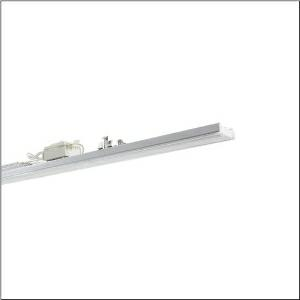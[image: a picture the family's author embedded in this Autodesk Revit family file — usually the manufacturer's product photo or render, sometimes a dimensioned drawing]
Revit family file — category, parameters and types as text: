
# Revit family: licross_21_recessed_mo_51te11vn48xg
name_source: partatom
category: Lighting Fixtures
units: mm (PartAtom-declared; Revit-internal decimal feet)

## family parameters
Cut with Voids When Loaded = No
Host = Face
Light Source = No
Part Type = Normal
Room Calculation Point = No
Round Connector Dimension = Use Diameter
Shared = No

## types (1)
- --- (1 x LED, 8000 lm, 44.1 W, 4000K)
    Apparent Load = 44 VA
    CIE Flux Codes = 89 96 99 100 100
    Color Rendering = 80
    Color Temperature = 4000K
    Default Elevation = 1800 mm
    Description = Licross 21 Recessed MO, luminaire insert, of sheet steel, galvanised, coil coated, white, length: 1.500mm, width: 66mm, height: 67mm, LED rated luminous flux: 8.000lm, light colour: 840, SDCM (Standard Deviation of Colour Matching)MacAdam ≤ 2 SDCM (initial), control gear: DALI 2, CLO, with plug, 5-pole, with phase selection, mains connection: 220..240V, AC, 50/60Hz, start of lifetime: 44W, end of service life: 48W, internal wiring halogen-free, primary light control with lens, of plastic, primary optical cover: cover, of PMMA, light emission: direct distribution, primary light characteristic: symmetric, protection rating (complete): IP54, insulation class (complete): insulation class I (protective earthing), certification: CE, ENEC, VDE, UKCA, protection symbol: D if used in an environment with non-conductive dust loads with corresponding accessories, impact resistance: IK06, permissible ambient temperature for indoor applications: -25..+35°C, corresponds to IFS (International Featured Standards) requirements for safety and quality in the food industry, reducing of maximum allowable ambient temperature of 5°C with ceiling mounting, LABS conformity tested according to VDMA 24364:2018-05, The light source and the operating device comply with the requirements of the Ecodesign Regulation (EU) 2019/2020 and are replaceable in accordance with this regulation, packaging unit: 1 piece
    Height = 58 mm
    Lamp = 1 x LED
    Lamp Light Flux = 8000 lm
    Lamp Power = 44.1 W
    Lamp count = 1
    Length = 1500 mm
    Luminous efficacy = 181 lm/W
    Manufacturer = Siteco
    ModVariant = No
    Model = 51TE11VN48XG
    Mounting Place = Ceiling
    Mounting Type = Pendant
    Number of Poles = 1
    OnlyDefault = Yes
    Power Factor = 1
    Product Name = Licross 21 Recessed MO
    Product group = luminaire insert | ceiling pendant
    ProductGroupID = 901
    Protection Class = Protection class I
    Protection Degree = IP 54
    RLX_Detail_Level = 1
    RLX_Emergency_Light_Flux = 0 lm
    RLX_Emergency_Type = 0
    RLX_Emergency_Type_DB = No
    RlxData = <blob elided: 24801 chars, md5=104b1db2>
    Socket = socket
    Standby Power = 0 W
    System Light Flux = 8000 lm
    System Power = 44 W
    Type Comments = factory setting: luminous flux: 100 % | dim-lin: 254 | 294 mA
    Type Image = l_1296930.jpg
    URL = http://relux.com
    VarID = @adj_092237
    Voltage = 0 V
    Weight = 0.00 kg
    Width = 66 mm

## geometry (parser evidence)
native form markers: Blend x4, Sweep x12
no freeform markers — native parametric forms only
